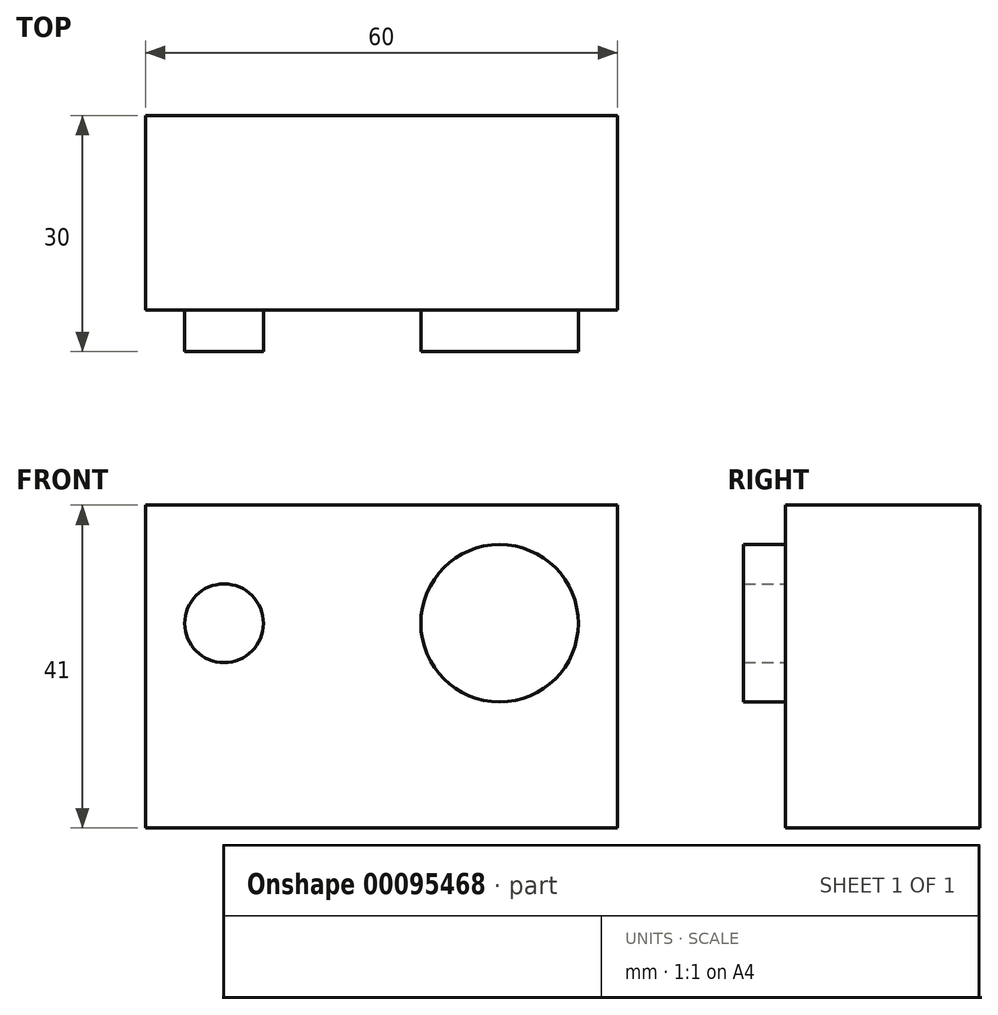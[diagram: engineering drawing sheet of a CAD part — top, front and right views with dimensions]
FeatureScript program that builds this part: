
annotation { "Feature Type Name" : "Feature", "Feature Type Description" : "" }
export const myFeature = defineFeature(function(context is Context, id is Id, definition is map)
    precondition{}
    {
        {
            var Q0;
            Q0=qCreatedBy(makeId("Front.planeOp"),FACE);
            var sketch = newSketch(context, id + "F0", { "sketchPlane" : qUnion([Q0])});
            skLineSegment(sketch, "E0.bottom", {"start": v(-30, 20.5) * mm, "end": v(30, 20.5) * mm});
            skLineSegment(sketch, "E0.top", {"start": v(-30, -20.5) * mm, "end": v(30, -20.5) * mm});
            skLineSegment(sketch, "E0.left", {"start": v(-30, 20.5) * mm, "end": v(-30, -20.5) * mm});
            skLineSegment(sketch, "E0.right", {"start": v(30, 20.5) * mm, "end": v(30, -20.5) * mm});
            skPoint(sketch, "E0.middle", {"position": v(0, 0) * mm});
            skSolve(sketch);
        }
        {
            var Q0;
            Q0 = qSketchRegion(id + "F0", true);
            extrude(context, id + "F1", {"entities" : qUnion([Q0]), "endBound" : BoundingType.SYMMETRIC, "depth" : 24.7 * mm});
        }
        {
            var Q0;
            Q0=makeQuery(id+"F1.opExtrude","CAP_FACE",FACE,{"disambiguationData":[OSD([sQuery(id+"F0.wireOp",EDGE,"E0.bottom"),sQuery(id+"F0.wireOp",EDGE,"E0.top"),sQuery(id+"F0.wireOp",EDGE,"E0.left"),sQuery(id+"F0.wireOp",EDGE,"E0.right")])],"isStart":false});
            var sketch = newSketch(context, id + "F2", { "sketchPlane" : qUnion([Q0])});
            skCircle(sketch, "E1", {"center": v(15, 5.5) * mm, "radius": 10 * mm});
            skCircle(sketch, "E2", {"center": v(-20, 5.5) * mm, "radius": 5 * mm});
            skSolve(sketch);
        }
        {
            var Q0;
            Q0 = qSketchRegion(id + "F2", true);
            extrude(context, id + "F3", {"entities" : qUnion([Q0]), "operationType" : NewBodyOperationType.ADD, "depth" : 5.3 * mm});
        }
    });
